# Revit family: 614406091_Mueble Aluvia Habano Elevado 60x45
name_source: partatom
category: Modelos genéricos
units: mm (PartAtom-declared; Revit-internal decimal feet)

## family parameters
Anfitrión = Muro
Compartido = No
Corte con vacíos al cargar = No
Cota de conector redondo = Diámetro de uso
Número OmniClass = 23.31.13.11
Puede alojar armadura = No
Punto de cálculo de habitación = No
Siempre vertical = Sí
Tipo de pieza = Normal
Título OmniClass = Single Sinks

## types (2) — shared parameters
Alto = 850 mm  [stored 2.78871 ft]
Ancho = 595 mm
Canto = PVC rígido 2 mm de calibre.
PVC Flexible 0,5 mm de calibre.
Carga Máxima = 110,2 lb (50 kg).
Creado por = IDD
Densidad = 15mm 670 kg./m^3.
Descripción = La línea ALUVIA viene a entregar de manera asequible una solución perfecta que combina
diseño y funcionalidad, ALUVIA se inspira en el movimiento y caída del agua en la
naturaleza, es por ello de sus formas orgánicas donde podemos obtener un producto
compacto y de líneas fluidas, que se adapta en espacios pequeños.
El principal beneficio de los muebles de esta línea es ser un producto compacto que brinda
al consumidor máxima capacidad de almacenamiento e ideal para espacios pequeños.
· Mueble compacto para espacios medianos.
· Lavamanos 100% en porcelana.
· Grán capacidad de almacenamiento.
· Resistentes a la Humedad.
Dimensiones Generales (H* W * P) = 21,85” x 23,46” x 17,52” (555 x 596 x 445 mm).
Fabricante = Corona
Fecha de creación = 22/07/2020
Garantía Herrajes = 1 año
Garantía Madera = 1 año
Material Piezas interiores = Corona_Madera_Aglomerada_Plomo
Peso Bruto aprox = 27,8 lb (12,6 kg).
Peso Neto aprox = 26,0 lb (11,8 kg).
Profundidad = 445 mm  [stored 1.45997 ft]
Resistencia a la humedad = 8%.
Resistencia al rayado = 700 ciclos.
Textura = Habano: Poro - Gris: Soft.
Tiempo de Armado = 80 Minutos.
URL = https://corona.co

## per-type parameters (varying)
| type | Material |
| Ref. 614401711 Mueble Elevado Aluvia Miel Con Lavamanos. | Corona_Madera_Aglomerada_Miel |
| Ref. 614406091 Mueble Elevado Aluvia Habano Con Lavamanos. | Corona_Madera_Aglomerada_Habano |

note: [stored X ft] marks values corroborated as IEEE doubles in the binary element streams (Revit-internal decimal feet)

## geometry (parser evidence)
native form markers: Blend x3, Extrusion x1, Sweep x8
no freeform markers — native parametric forms only
